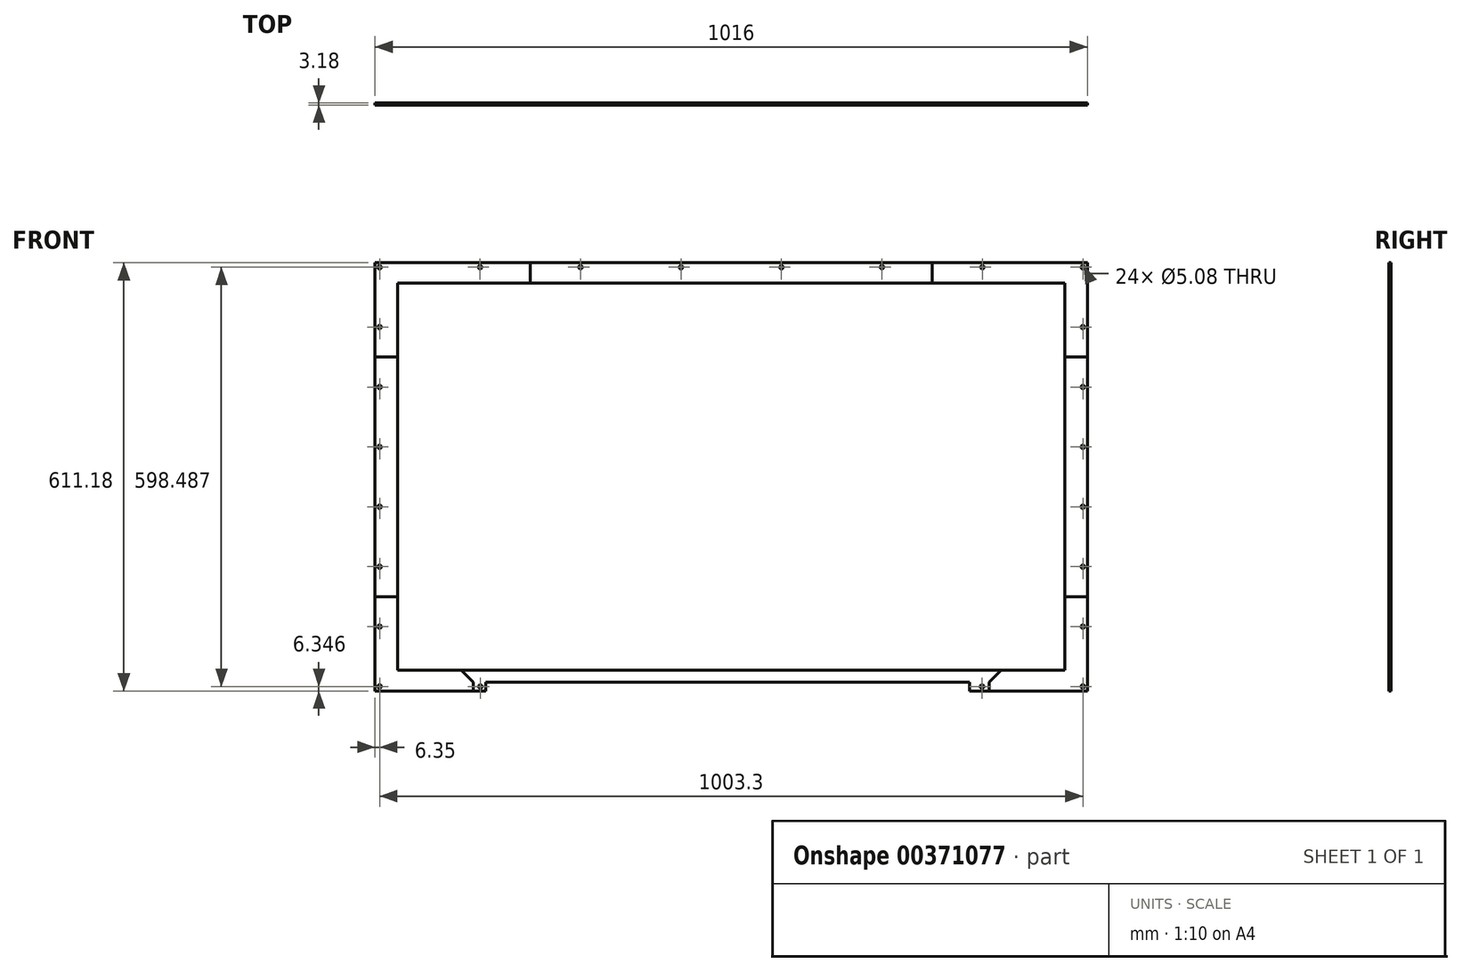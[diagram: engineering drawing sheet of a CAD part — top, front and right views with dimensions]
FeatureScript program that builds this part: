
annotation { "Feature Type Name" : "Feature", "Feature Type Description" : "" }
export const myFeature = defineFeature(function(context is Context, id is Id, definition is map)
    precondition{}
    {
        {
            var Q0;
            Q0=qCreatedBy(makeId("Front.planeOp"),FACE);
            var sketch = newSketch(context, id + "F0", { "sketchPlane" : qUnion([Q0])});
            skLineSegment(sketch, "E0.bottom", {"start": v(495.3, 292.9) * mm, "end": v(-495.3, 292.9) * mm});
            skLineSegment(sketch, "E0.top", {"start": v(495.3, -292.9) * mm, "end": v(-495.3, -292.9) * mm});
            skLineSegment(sketch, "E0.left", {"start": v(495.3, 292.9) * mm, "end": v(495.3, -292.9) * mm});
            skLineSegment(sketch, "E0.right", {"start": v(-495.3, 292.9) * mm, "end": v(-495.3, -292.9) * mm});
            skPoint(sketch, "E0.middle", {"position": v(0, 0) * mm});
            skLineSegment(sketch, "E1.0", {"start": v(-508, 305.6) * mm, "end": v(-508, -305.6) * mm});
            skLineSegment(sketch, "E1.1", {"start": v(508, 305.6) * mm, "end": v(-508, 305.6) * mm});
            skLineSegment(sketch, "E1.2", {"start": v(508, 305.6) * mm, "end": v(508, -305.6) * mm});
            skLineSegment(sketch, "E2", {"start": v(-508, 305.6) * mm, "end": v(-495.3, 292.9) * mm});
            skPoint(sketch, "E3.middle", {"position": v(-501.65, 299.24) * mm});
            skLineSegment(sketch, "E4", {"start": v(-350.3, -292.9) * mm, "end": v(-350.3, -305.6) * mm});
            skLineSegment(sketch, "E5", {"start": v(340.3, -292.9) * mm, "end": v(340.3, -305.6) * mm});
            skLineSegment(sketch, "E6.bottom", {"start": v(476, 276.23) * mm, "end": v(-476, 276.23) * mm});
            skLineSegment(sketch, "E6.top", {"start": v(476, -276.22) * mm, "end": v(-476, -276.23) * mm});
            skLineSegment(sketch, "E6.left", {"start": v(476, 276.23) * mm, "end": v(476, -276.23) * mm});
            skLineSegment(sketch, "E6.right", {"start": v(-476, 276.23) * mm, "end": v(-476, -276.23) * mm});
            skLineSegment(sketch, "E7", {"start": v(-508, -305.6) * mm, "end": v(-350.3, -305.6) * mm});
            skLineSegment(sketch, "E8", {"start": v(340.3, -305.6) * mm, "end": v(508, -305.6) * mm});
            skLineSegment(sketch, "E9", {"start": v(-495.3, -292.9) * mm, "end": v(-508, -305.6) * mm});
            skPoint(sketch, "E10", {"position": v(-501.65, -299.24) * mm});
            skCircle(sketch, "E11", {"center": v(-501.65, 299.24) * mm, "radius": 2.54 * mm});
            skCircle(sketch, "E12", {"center": v(-358.32, 299.24) * mm, "radius": 2.54 * mm});
            skCircle(sketch, "E13", {"center": v(-215, 299.24) * mm, "radius": 2.54 * mm});
            skCircle(sketch, "E14", {"center": v(-71.66, 299.24) * mm, "radius": 2.54 * mm});
            skCircle(sketch, "E15", {"center": v(71.66, 299.24) * mm, "radius": 2.54 * mm});
            skCircle(sketch, "E16", {"center": v(215, 299.24) * mm, "radius": 2.54 * mm});
            skCircle(sketch, "E17", {"center": v(-501.65, 213.75) * mm, "radius": 2.54 * mm});
            skCircle(sketch, "E18", {"center": v(-501.65, 128.25) * mm, "radius": 2.54 * mm});
            skCircle(sketch, "E19", {"center": v(-501.65, 42.75) * mm, "radius": 2.54 * mm});
            skCircle(sketch, "E20", {"center": v(-501.65, -42.75) * mm, "radius": 2.54 * mm});
            skCircle(sketch, "E21", {"center": v(358.32, 299.24) * mm, "radius": 2.54 * mm});
            skCircle(sketch, "E22", {"center": v(501.65, 299.24) * mm, "radius": 2.54 * mm});
            skCircle(sketch, "E23", {"center": v(501.65, 213.75) * mm, "radius": 2.54 * mm});
            skCircle(sketch, "E24", {"center": v(501.65, 128.25) * mm, "radius": 2.54 * mm});
            skCircle(sketch, "E25", {"center": v(501.65, 42.75) * mm, "radius": 2.54 * mm});
            skCircle(sketch, "E26", {"center": v(501.65, -42.75) * mm, "radius": 2.54 * mm});
            skCircle(sketch, "E27", {"center": v(501.65, -128.25) * mm, "radius": 2.54 * mm});
            skCircle(sketch, "E28", {"center": v(501.65, -213.75) * mm, "radius": 2.54 * mm});
            skCircle(sketch, "E29", {"center": v(501.65, -299.24) * mm, "radius": 2.54 * mm});
            skCircle(sketch, "E30", {"center": v(357.84, -299.24) * mm, "radius": 2.54 * mm});
            skCircle(sketch, "E31", {"center": v(-357.84, -299.24) * mm, "radius": 2.54 * mm});
            skCircle(sketch, "E32", {"center": v(-501.65, -299.24) * mm, "radius": 2.54 * mm});
            skCircle(sketch, "E33", {"center": v(-501.65, -213.75) * mm, "radius": 2.54 * mm});
            skCircle(sketch, "E34", {"center": v(-501.65, -128.25) * mm, "radius": 2.54 * mm});
            skLineSegment(sketch, "E35", {"start": v(-358.32, 299.24) * mm, "end": v(-215, 299.24) * mm});
            skLineSegment(sketch, "E36", {"start": v(-286.66, 305.6) * mm, "end": v(-286.66, 276.23) * mm});
            skPoint(sketch, "E36.startSnap0", {"position": v(-286.66, 299.24) * mm});
            skLineSegment(sketch, "E37.MirrorCS", {"start": v(286.66, 305.6) * mm, "end": v(286.66, 276.23) * mm});
            skLineSegment(sketch, "E38", {"start": v(-501.65, 213.75) * mm, "end": v(-501.65, 128.25) * mm});
            skLineSegment(sketch, "E39", {"start": v(-508, 171) * mm, "end": v(-476, 171) * mm});
            skPoint(sketch, "E39.startSnap0", {"position": v(-501.65, 171) * mm});
            skLineSegment(sketch, "E40.MirrorCS", {"start": v(-508, -171) * mm, "end": v(-476, -171) * mm});
            skLineSegment(sketch, "E41.MirrorCS", {"start": v(508, -171) * mm, "end": v(476, -171) * mm});
            skLineSegment(sketch, "E42.MirrorCS", {"start": v(508, 171) * mm, "end": v(476, 171) * mm});
            skLineSegment(sketch, "E43", {"start": v(368.3, -305.6) * mm, "end": v(368.3, -292.9) * mm});
            skLineSegment(sketch, "E44.MirrorCS", {"start": v(-368.3, -305.6) * mm, "end": v(-368.3, -292.9) * mm});
            skLineSegment(sketch, "E45", {"start": v(368.3, -292.9) * mm, "end": v(384.97, -276.22) * mm});
            skLineSegment(sketch, "E46.MirrorCS", {"start": v(-368.3, -292.9) * mm, "end": v(-384.97, -276.22) * mm});
            skSolve(sketch);
        }
        {
            var Q0;
            {var subQ7=sQuery(id+"F0.wireOp",EDGE,"E6.right");var subQ8=sQuery(id+"F0.wireOp",EDGE,"E6.bottom");var subQ9=makeQuery(id+"F0.imprint","INTERSECT",VERTEX,{"derivedFrom":[subQ8,subQ7]});Q0=makeQuery(id+"F0.imprint","IMPRINT",FACE,{"disambiguationData":[TD([[makeQuery(id+"F0.imprint","IMPRINT",EDGE,{"disambiguationData":[TD([[subQ9,1.0]])],"derivedFrom":subQ8}),-1.0]])]});}
            var Q1;
            Q1=makeQuery(id+"F0.imprint","IMPRINT",FACE,{"disambiguationData":[TD([[makeQuery(id+"F0.imprint","IMPRINT",EDGE,{"derivedFrom":sQuery(id+"F0.wireOp",EDGE,"E17")}),-1.0]])]});
            var Q2;
            Q2=makeQuery(id+"F0.imprint","IMPRINT",FACE,{"disambiguationData":[TD([[makeQuery(id+"F0.imprint","IMPRINT",EDGE,{"derivedFrom":sQuery(id+"F0.wireOp",EDGE,"E12")}),-1.0]])]});
            extrude(context, id + "F1", {"entities" : qUnion([Q0, Q1, Q2]), "endBound" : BoundingType.SYMMETRIC, "depth" : 3.17 * mm});
        }
        {
            var Q0;
            {var subQ0=sQuery(id+"F0.wireOp",EDGE,"E37.MirrorCS");var subQ1=sQuery(id+"F0.wireOp",EDGE,"E0.bottom");var subQ2=makeQuery(id+"F0.imprint","INTERSECT",VERTEX,{"derivedFrom":[subQ1,subQ0]});Q0=makeQuery(id+"F0.imprint","IMPRINT",FACE,{"disambiguationData":[TD([[makeQuery(id+"F0.imprint","IMPRINT",EDGE,{"disambiguationData":[TD([[subQ2,-1.0]])],"derivedFrom":subQ1}),1.0]])]});}
            var Q1;
            Q1=makeQuery(id+"F0.imprint","IMPRINT",FACE,{"disambiguationData":[TD([[makeQuery(id+"F0.imprint","IMPRINT",EDGE,{"derivedFrom":sQuery(id+"F0.wireOp",EDGE,"E13")}),-1.0]])]});
            extrude(context, id + "F2", {"entities" : qUnion([Q0, Q1]), "endBound" : BoundingType.SYMMETRIC, "depth" : 3.17 * mm});
        }
        {
            var Q0;
            {var subQ7=sQuery(id+"F0.wireOp",EDGE,"E0.left");var subQ8=sQuery(id+"F0.wireOp",EDGE,"E0.bottom");var subQ9=makeQuery(id+"F0.imprint","INTERSECT",VERTEX,{"derivedFrom":[subQ8,subQ7]});Q0=makeQuery(id+"F0.imprint","IMPRINT",FACE,{"disambiguationData":[TD([[makeQuery(id+"F0.imprint","IMPRINT",EDGE,{"disambiguationData":[TD([[subQ9,-1.0]])],"derivedFrom":subQ8}),1.0]])]});}
            var Q1;
            Q1=makeQuery(id+"F0.imprint","IMPRINT",FACE,{"disambiguationData":[TD([[makeQuery(id+"F0.imprint","IMPRINT",EDGE,{"derivedFrom":sQuery(id+"F0.wireOp",EDGE,"E21")}),-1.0]])]});
            extrude(context, id + "F3", {"entities" : qUnion([Q0, Q1]), "endBound" : BoundingType.SYMMETRIC, "depth" : 3.17 * mm});
        }
        {
            var Q0;
            {var subQ0=sQuery(id+"F0.wireOp",EDGE,"E42.MirrorCS");var subQ1=sQuery(id+"F0.wireOp",EDGE,"E0.left");var subQ2=makeQuery(id+"F0.imprint","INTERSECT",VERTEX,{"derivedFrom":[subQ1,subQ0]});Q0=makeQuery(id+"F0.imprint","IMPRINT",FACE,{"disambiguationData":[TD([[makeQuery(id+"F0.imprint","IMPRINT",EDGE,{"disambiguationData":[TD([[subQ2,-1.0]])],"derivedFrom":subQ1}),-1.0]])]});}
            var Q1;
            Q1=makeQuery(id+"F0.imprint","IMPRINT",FACE,{"disambiguationData":[TD([[makeQuery(id+"F0.imprint","IMPRINT",EDGE,{"derivedFrom":sQuery(id+"F0.wireOp",EDGE,"E24")}),-1.0]])]});
            extrude(context, id + "F4", {"entities" : qUnion([Q0, Q1]), "endBound" : BoundingType.SYMMETRIC, "depth" : 3.17 * mm});
        }
        {
            var Q0;
            {var subQ0=sQuery(id+"F0.wireOp",EDGE,"X4arY4AP-lXZk-l7Nx-RXXv-BhhCrD5j1vKJ");Q0=makeQuery(id+"F0.imprint","IMPRINT",FACE,{"disambiguationData":[TD([[makeQuery(id+"F0.imprint","IMPRINT",EDGE,{"derivedFrom":subQ0}),-1.0]])]});}
            var Q1;
            Q1=makeQuery(id+"F0.imprint","IMPRINT",FACE,{"disambiguationData":[TD([[makeQuery(id+"F0.imprint","IMPRINT",EDGE,{"derivedFrom":sQuery(id+"F0.wireOp",EDGE,"E28")}),-1.0]])]});
            var Q2;
            {var subQ0=sQuery(id+"F0.wireOp",EDGE,"X4arY4AP-lXZk-l7Nx-RXXv-BhhCrD5j1vKJ");Q2=makeQuery(id+"F0.imprint","IMPRINT",FACE,{"disambiguationData":[TD([[makeQuery(id+"F0.imprint","IMPRINT",EDGE,{"derivedFrom":subQ0}),1.0]])]});}
            var Q3;
            {var subQ8=sQuery(id+"F0.wireOp",EDGE,"E45");Q3=makeQuery(id+"F0.imprint","IMPRINT",FACE,{"disambiguationData":[TD([[makeQuery(id+"F0.imprint","IMPRINT",EDGE,{"derivedFrom":subQ8}),-1.0]])]});}
            extrude(context, id + "F5", {"entities" : qUnion([Q0, Q1, Q2, Q3]), "endBound" : BoundingType.SYMMETRIC, "depth" : 3.17 * mm});
        }
        {
            var Q0;
            {var subQ0=sQuery(id+"F0.wireOp",EDGE,"E45");Q0=makeQuery(id+"F0.imprint","IMPRINT",FACE,{"disambiguationData":[TD([[makeQuery(id+"F0.imprint","IMPRINT",EDGE,{"derivedFrom":subQ0}),1.0]])]});}
            var Q1;
            {var subQ1=sQuery(id+"F0.wireOp",EDGE,"E5");Q1=makeQuery(id+"F0.imprint","IMPRINT",FACE,{"disambiguationData":[TD([[makeQuery(id+"F0.imprint","IMPRINT",EDGE,{"derivedFrom":subQ1}),1.0]])]});}
            var Q2;
            {var subQ1=sQuery(id+"F0.wireOp",EDGE,"E4");Q2=makeQuery(id+"F0.imprint","IMPRINT",FACE,{"disambiguationData":[TD([[makeQuery(id+"F0.imprint","IMPRINT",EDGE,{"derivedFrom":subQ1}),-1.0]])]});}
            extrude(context, id + "F6", {"entities" : qUnion([Q0, Q1, Q2]), "endBound" : BoundingType.SYMMETRIC, "depth" : 3.17 * mm});
        }
        {
            var Q0;
            {var subQ3=sQuery(id+"F0.wireOp",EDGE,"E44.MirrorCS");Q0=makeQuery(id+"F0.imprint","IMPRINT",FACE,{"disambiguationData":[TD([[makeQuery(id+"F0.imprint","IMPRINT",EDGE,{"derivedFrom":subQ3}),1.0]])]});}
            var Q1;
            {var subQ7=sQuery(id+"F0.wireOp",EDGE,"b2e545cd-ef14-445c-9ec2-2e71257f41a00.MirrorCS");Q1=makeQuery(id+"F0.imprint","IMPRINT",FACE,{"disambiguationData":[TD([[makeQuery(id+"F0.imprint","IMPRINT",EDGE,{"derivedFrom":subQ7}),-1.0]])]});}
            var Q2;
            Q2=makeQuery(id+"F0.imprint","IMPRINT",FACE,{"disambiguationData":[TD([[makeQuery(id+"F0.imprint","IMPRINT",EDGE,{"derivedFrom":sQuery(id+"F0.wireOp",EDGE,"E33")}),-1.0]])]});
            var Q3;
            {var subQ5=sQuery(id+"F0.wireOp",EDGE,"E46.MirrorCS");Q3=makeQuery(id+"F0.imprint","IMPRINT",FACE,{"disambiguationData":[TD([[makeQuery(id+"F0.imprint","IMPRINT",EDGE,{"derivedFrom":subQ5}),1.0]])]});}
            extrude(context, id + "F7", {"entities" : qUnion([Q0, Q1, Q2, Q3]), "endBound" : BoundingType.SYMMETRIC, "depth" : 3.17 * mm});
        }
        {
            var Q0;
            {var subQ0=sQuery(id+"F0.wireOp",EDGE,"E39");var subQ1=sQuery(id+"F0.wireOp",EDGE,"E0.right");var subQ2=makeQuery(id+"F0.imprint","INTERSECT",VERTEX,{"derivedFrom":[subQ1,subQ0]});Q0=makeQuery(id+"F0.imprint","IMPRINT",FACE,{"disambiguationData":[TD([[makeQuery(id+"F0.imprint","IMPRINT",EDGE,{"disambiguationData":[TD([[subQ2,-1.0]])],"derivedFrom":subQ1}),1.0]])]});}
            var Q1;
            Q1=makeQuery(id+"F0.imprint","IMPRINT",FACE,{"disambiguationData":[TD([[makeQuery(id+"F0.imprint","IMPRINT",EDGE,{"derivedFrom":sQuery(id+"F0.wireOp",EDGE,"E18")}),-1.0]])]});
            extrude(context, id + "F8", {"entities" : qUnion([Q0, Q1]), "endBound" : BoundingType.SYMMETRIC, "depth" : 3.17 * mm});
        }
    });
